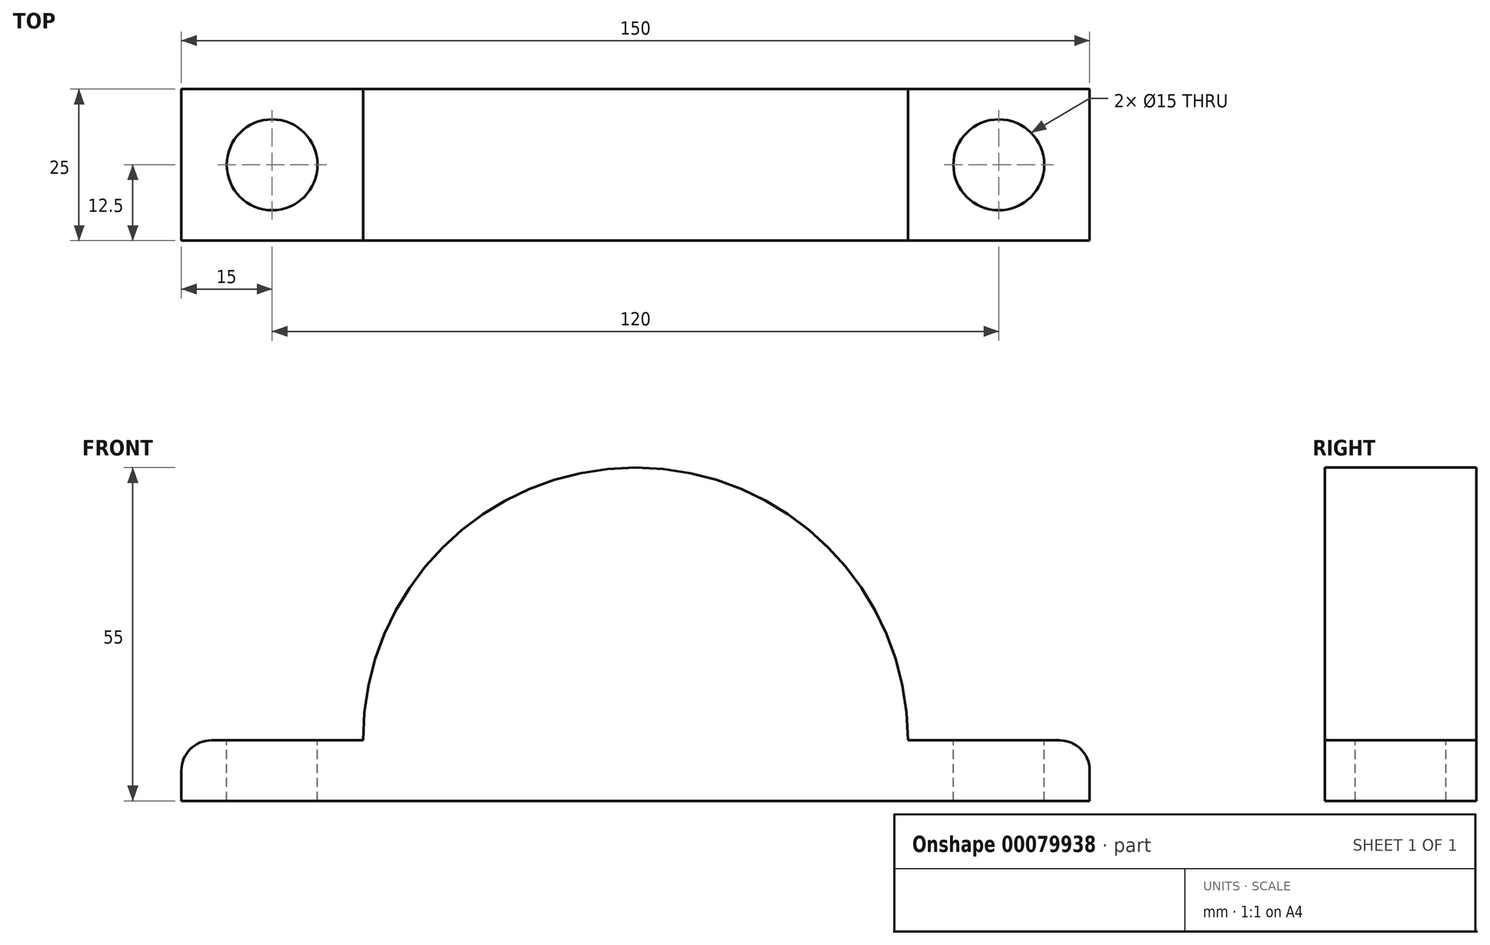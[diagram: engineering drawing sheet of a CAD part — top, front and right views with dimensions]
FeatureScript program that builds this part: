
annotation { "Feature Type Name" : "Feature", "Feature Type Description" : "" }
export const myFeature = defineFeature(function(context is Context, id is Id, definition is map)
    precondition{}
    {
        {
            var Q0;
            Q0=qCreatedBy(makeId("Front.planeOp"),FACE);
            var sketch = newSketch(context, id + "F0", { "sketchPlane" : qUnion([Q0])});
            skLineSegment(sketch, "E0", {"start": v(-75, 0) * mm, "end": v(-75, 5) * mm});
            skLineSegment(sketch, "E1", {"start": v(-45, 10) * mm, "end": v(-45, 0) * mm});
            skLineSegment(sketch, "E2", {"start": v(-45, 0) * mm, "end": v(-75, 0) * mm});
            skLineSegment(sketch, "E3", {"start": v(-70, 10) * mm, "end": v(-45, 10) * mm});
            skLineSegment(sketch, "E4.MirrorCS", {"start": v(70, 10) * mm, "end": v(45, 10) * mm});
            skLineSegment(sketch, "E5.MirrorCS", {"start": v(45, 10) * mm, "end": v(45, 0) * mm});
            skLineSegment(sketch, "E6.MirrorCS", {"start": v(45, 0) * mm, "end": v(75, 0) * mm});
            skLineSegment(sketch, "E7.MirrorCS", {"start": v(75, 0) * mm, "end": v(75, 5) * mm});
            skPoint(sketch, "E8.visualSharp", {"position": v(-75, 10) * mm});
            skArc(sketch, "E8.filletArc", {"start": v(-70, 10) * mm, "mid": v(-73.54, 8.54) * mm, "end": v(-75, 5) * mm});
            skPoint(sketch, "E9.visualSharp", {"position": v(75, 10) * mm});
            skArc(sketch, "E9.filletArc", {"start": v(75, 5) * mm, "mid": v(73.54, 8.54) * mm, "end": v(70, 10) * mm});
            skLineSegment(sketch, "E10.bottom", {"start": v(-45, 0) * mm, "end": v(45, 0) * mm});
            skLineSegment(sketch, "E10.top", {"start": v(0, 55) * mm, "end": v(0, 55) * mm});
            skLineSegment(sketch, "E10.left", {"start": v(-45, 0) * mm, "end": v(-45, 10) * mm});
            skLineSegment(sketch, "E10.right", {"start": v(45, 0) * mm, "end": v(45, 10) * mm});
            skPoint(sketch, "E11.visualSharp", {"position": v(-45, 55) * mm});
            skArc(sketch, "E11.filletArc", {"start": v(0, 55) * mm, "mid": v(-31.82, 41.82) * mm, "end": v(-45, 10) * mm});
            skPoint(sketch, "E12.visualSharp", {"position": v(45, 55) * mm});
            skArc(sketch, "E12.filletArc", {"start": v(45, 10) * mm, "mid": v(31.82, 41.82) * mm, "end": v(0, 55) * mm});
            skSolve(sketch);
        }
        {
            var Q0;
            Q0=makeQuery(id+"F0.imprint","IMPRINT",FACE,{"disambiguationData":[TD([[makeQuery(id+"F0.imprint","IMPRINT",EDGE,{"derivedFrom":sQuery(id+"F0.wireOp",EDGE,"E10.bottom")}),1.0]])]});
            var Q1;
            Q1=makeQuery(id+"F0.imprint","IMPRINT",FACE,{"disambiguationData":[TD([[makeQuery(id+"F0.imprint","IMPRINT",EDGE,{"derivedFrom":sQuery(id+"F0.wireOp",EDGE,"E0")}),-1.0]])]});
            var Q2;
            Q2=makeQuery(id+"F0.imprint","IMPRINT",FACE,{"disambiguationData":[TD([[makeQuery(id+"F0.imprint","IMPRINT",EDGE,{"derivedFrom":sQuery(id+"F0.wireOp",EDGE,"E4.MirrorCS")}),1.0]])]});
            extrude(context, id + "F1", {"entities" : qUnion([Q0, Q1, Q2]), "depth" : 25 * mm});
        }
        {
            var Q0;
            Q0=makeQuery(id+"F1.opExtrude","SWEPT_FACE",FACE,{"disambiguationData":[OSD([sQuery(id+"F0.wireOp",EDGE,"E3")])]});
            var sketch = newSketch(context, id + "F2", { "sketchPlane" : qUnion([Q0])});
            skCircle(sketch, "E13", {"center": v(-60, -12.5) * mm, "radius": 7.5 * mm});
            skCircle(sketch, "E14.MirrorC", {"center": v(60, -12.5) * mm, "radius": 7.5 * mm});
            skSolve(sketch);
        }
        {
            var Q0;
            Q0 = qSketchRegion(id + "F2", true);
            extrude(context, id + "F3", {"entities" : qUnion([Q0]), "operationType" : NewBodyOperationType.REMOVE, "endBound" : BoundingType.THROUGH_ALL, "oppositeDirection" : true, "depth" : 25 * mm});
        }
    });
